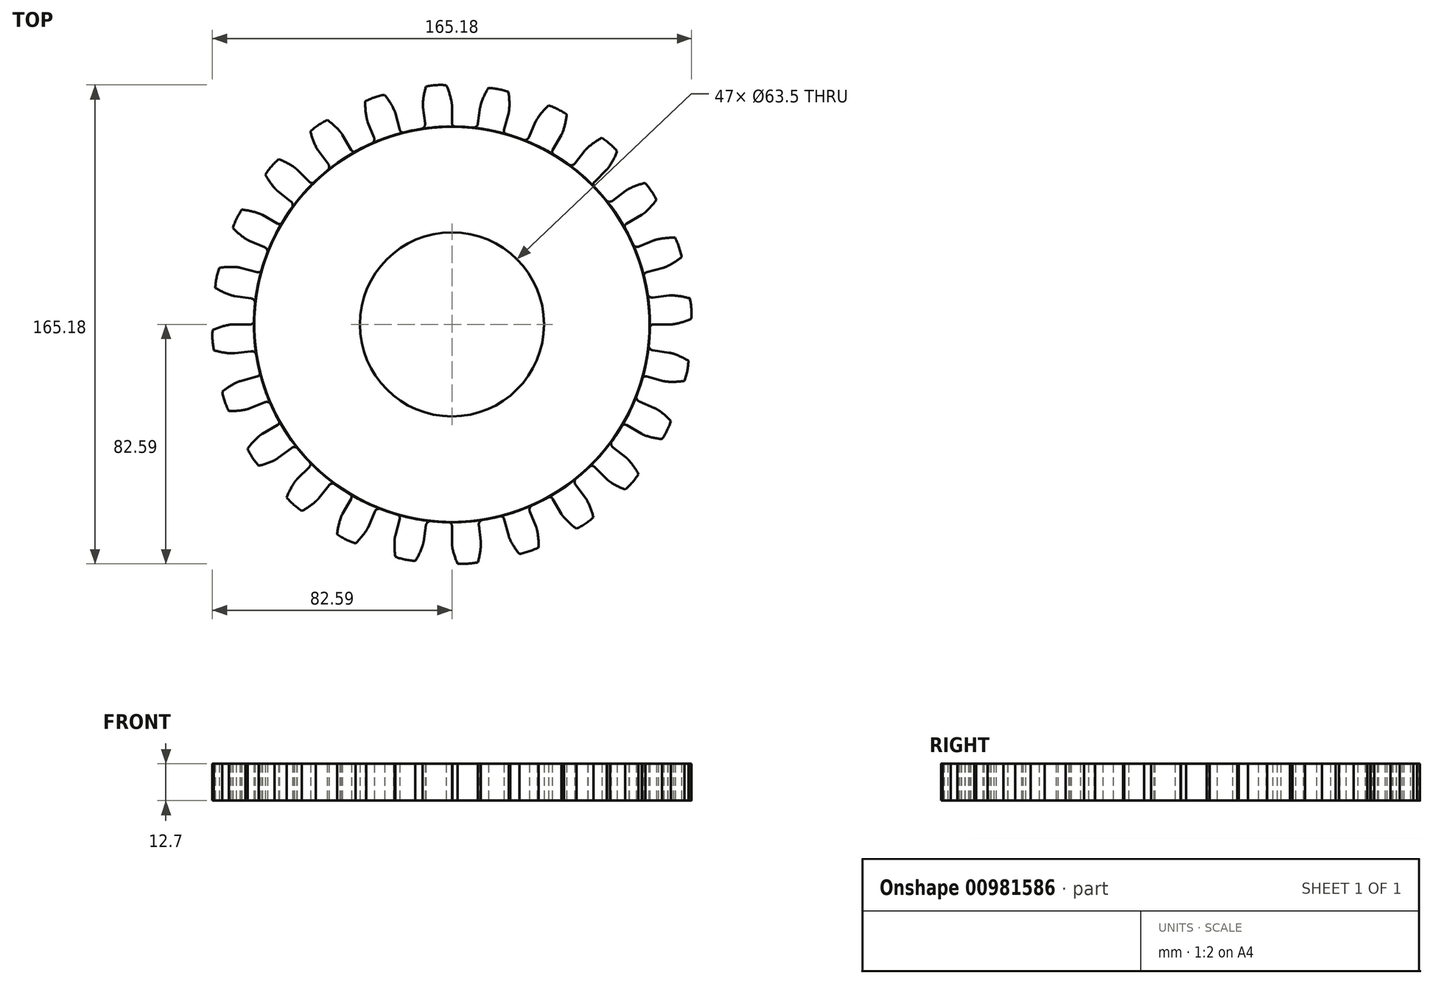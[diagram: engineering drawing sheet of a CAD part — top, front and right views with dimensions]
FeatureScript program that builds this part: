
annotation { "Feature Type Name" : "Feature", "Feature Type Description" : "" }
export const myFeature = defineFeature(function(context is Context, id is Id, definition is map)
    precondition{}
    {
        {
            var Q0;
            Q0=qCreatedBy(makeId("Top.planeOp"),FACE);
            var sketch = newSketch(context, id + "F0", { "sketchPlane" : qUnion([Q0])});
            skCircle(sketch, "E0", {"center": v(0, 0) * mm, "radius": 68.24 * mm});
            skCircle(sketch, "E1", {"center": v(0, 0) * mm, "radius": 76.2 * mm, "construction": true});
            skCircle(sketch, "E2", {"center": v(0, 0) * mm, "radius": 82.55 * mm, "construction": true});
            skLineSegment(sketch, "E3", {"start": v(0, 0) * mm, "end": v(0, 97.16) * mm, "construction": true});
            skLineSegment(sketch, "E4", {"start": v(0, 0) * mm, "end": v(-6.33, 96.56) * mm, "construction": true});
            skCircle(sketch, "E5", {"center": v(0, 0) * mm, "radius": 69.84 * mm, "construction": true});
            skCircle(sketch, "E6", {"center": v(0, 0) * mm, "radius": 75.54 * mm, "construction": true});
            skLineSegment(sketch, "E7", {"start": v(0, 0) * mm, "end": v(-12.68, 96.32) * mm, "construction": true});
            skLineSegment(sketch, "E8", {"start": v(0, 0) * mm, "end": v(-19.06, 95.82) * mm, "construction": true});
            skLineSegment(sketch, "E9", {"start": v(-4.94, 75.38) * mm, "end": v(0, 75.7) * mm, "construction": true});
            skPoint(sketch, "E10", {"position": v(-4.93, 75.38) * mm});
            skPoint(sketch, "E11", {"position": v(-4.94, 75.38) * mm});
            skLineSegment(sketch, "E12", {"start": v(-4.94, 75.38) * mm, "end": v(0, 75.54) * mm, "construction": true});
            skPoint(sketch, "E13", {"position": v(-9.86, 74.9) * mm});
            skLineSegment(sketch, "E14", {"start": v(-9.86, 74.9) * mm, "end": v(-0.04, 76.19) * mm, "construction": true});
            skLineSegment(sketch, "E15", {"start": v(-14.74, 74.09) * mm, "end": v(-0.16, 76.99) * mm, "construction": true});
            skArc(sketch, "E16", {"start": v(0, 75.7) * mm, "mid": v(-0.01, 75.94) * mm, "end": v(-0.04, 76.19) * mm});
            skArc(sketch, "E17", {"start": v(-0.04, 76.19) * mm, "mid": v(-0.1, 76.59) * mm, "end": v(-0.16, 76.99) * mm});
            skLineSegment(sketch, "E18", {"start": v(-0.04, 76.19) * mm, "end": v(-0.05, 76.26) * mm, "construction": true});
            skLineSegment(sketch, "E19", {"start": v(0, 75.7) * mm, "end": v(0, 75.86) * mm, "construction": true});
            skArc(sketch, "E20", {"start": v(0, 75.54) * mm, "mid": v(0, 75.62) * mm, "end": v(0, 75.7) * mm});
            skArc(sketch, "E21", {"start": v(-0.16, 76.99) * mm, "mid": v(-0.9, 79.8) * mm, "end": v(-1.95, 82.53) * mm});
            skLineSegment(sketch, "E22", {"start": v(-0.16, 76.99) * mm, "end": v(-0.27, 77.5) * mm, "construction": true});
            skPoint(sketch, "E23", {"position": v(-9.96, 74.88) * mm});
            skPoint(sketch, "E24", {"position": v(-4.99, 75.37) * mm});
            skLineSegment(sketch, "E25", {"start": v(0, 0) * mm, "end": v(-4.99, 75.37) * mm, "construction": true});
            skArc(sketch, "E26.MirrorCS", {"start": v(-9.98, 76.34) * mm, "mid": v(-9.63, 79.23) * mm, "end": v(-8.95, 82.06) * mm});
            skArc(sketch, "E27.MirrorCS", {"start": v(-10, 75.53) * mm, "mid": v(-10, 75.93) * mm, "end": v(-9.98, 76.34) * mm});
            skArc(sketch, "E28.MirrorCS", {"start": v(-9.98, 75.04) * mm, "mid": v(-10, 75.28) * mm, "end": v(-10, 75.53) * mm});
            skArc(sketch, "E29", {"start": v(-9.98, 75.04) * mm, "mid": v(-9.97, 74.96) * mm, "end": v(-9.96, 74.88) * mm});
            skLineSegment(sketch, "E30", {"start": v(-9.96, 74.88) * mm, "end": v(-9.26, 69.23) * mm});
            skLineSegment(sketch, "E31", {"start": v(0, 75.54) * mm, "end": v(0, 69.84) * mm});
            skArc(sketch, "E32", {"start": v(-1.95, 82.53) * mm, "mid": v(-5.5, 83) * mm, "end": v(-8.95, 82.06) * mm});
            skSolve(sketch);
        }
        {
            var Q0;
            Q0 = qSketchRegion(id + "F0", true);
            extrude(context, id + "F1", {"entities" : qUnion([Q0]), "depth" : 12.7 * mm, "offsetDistance" : 25.4 * mm});
        }
        {
            var Q0;
            Q0=qCreatedBy(makeId("Top.planeOp"),FACE);
            var sketch = newSketch(context, id + "F2", { "sketchPlane" : qUnion([Q0])});
            skArc(sketch, "E33", {"start": v(0, 75.7) * mm, "mid": v(-0.01, 75.94) * mm, "end": v(-0.04, 76.19) * mm});
            skArc(sketch, "E34", {"start": v(-0.04, 76.19) * mm, "mid": v(-0.1, 76.59) * mm, "end": v(-0.16, 76.99) * mm});
            skArc(sketch, "E35", {"start": v(0, 75.54) * mm, "mid": v(0, 75.62) * mm, "end": v(0, 75.7) * mm});
            skArc(sketch, "E36", {"start": v(-0.16, 76.99) * mm, "mid": v(-0.9, 79.8) * mm, "end": v(-1.95, 82.53) * mm});
            skArc(sketch, "E37.MirrorCS", {"start": v(-9.98, 76.34) * mm, "mid": v(-9.63, 79.23) * mm, "end": v(-8.95, 82.06) * mm});
            skArc(sketch, "E38.MirrorCS", {"start": v(-10, 75.53) * mm, "mid": v(-10, 75.93) * mm, "end": v(-9.98, 76.34) * mm});
            skArc(sketch, "E39.MirrorCS", {"start": v(-9.98, 75.04) * mm, "mid": v(-10, 75.28) * mm, "end": v(-10, 75.53) * mm});
            skArc(sketch, "E40", {"start": v(-9.98, 75.04) * mm, "mid": v(-9.97, 74.96) * mm, "end": v(-9.96, 74.88) * mm});
            skLineSegment(sketch, "E41", {"start": v(-9.97, 74.94) * mm, "end": v(-9.26, 69.27) * mm});
            skLineSegment(sketch, "E42", {"start": v(0, 75.54) * mm, "end": v(0, 69.51) * mm});
            skArc(sketch, "E43", {"start": v(-1.95, 82.53) * mm, "mid": v(-5.46, 82.54) * mm, "end": v(-8.95, 82.06) * mm});
            skArc(sketch, "E44", {"start": v(-10.67, 67.4) * mm, "mid": v(-9.59, 68.05) * mm, "end": v(-9.26, 69.27) * mm});
            skArc(sketch, "E45", {"start": v(0, 69.51) * mm, "mid": v(0.37, 68.61) * mm, "end": v(1.26, 68.23) * mm});
            skCircle(sketch, "E46.0", {"center": v(0, 0) * mm, "radius": 68.24 * mm});
            skSolve(sketch);
        }
        {
            var Q0;
            Q0=makeQuery(id+"F2.imprint","IMPRINT",FACE,{"disambiguationData":[TD([[makeQuery(id+"F2.imprint","IMPRINT",EDGE,{"derivedFrom":sQuery(id+"F2.wireOp",EDGE,"E33")}),1.0]])]});
            extrude(context, id + "F3", {"entities" : qUnion([Q0]), "operationType" : NewBodyOperationType.ADD, "depth" : 12.7 * mm, "offsetDistance" : 25.4 * mm});
        }
        {
            var Q0;
            Q0=makeQuery(id+"F1.opExtrude","SWEPT_BODY",BODY,{"disambiguationData":[OSD([sQuery(id+"F0.wireOp",EDGE,"E0")])]});
            var Q1;
            Q1=makeQuery(id+"F1.opExtrude","SWEPT_FACE",FACE,{"disambiguationData":[OSD([sQuery(id+"F0.wireOp",EDGE,"E0")])]});
            circularPattern(context, id + "F4", {"entities" : qUnion([Q0]), "axis" : qUnion([Q1]), "angle" : 360 * degree, "instanceCount" : 24, "equalSpace" : true, "isCentered" : true});
        }
        {
            var Q0;
            Q0=sQuery(id+"F0.wireOp",VERTEX,"E3.start");
            var Q1;
            Q1=makeQuery(id+"F1.opExtrude","SWEPT_BODY",BODY,{"disambiguationData":[OSD([sQuery(id+"F0.wireOp",EDGE,"E0")])]});
            var Q2;
            Q2=makeQuery(id+"F4.opPattern","COPY",BODY,{"derivedFrom":makeQuery(id+"F1.opExtrude","SWEPT_BODY",BODY,{"disambiguationData":[OSD([sQuery(id+"F0.wireOp",EDGE,"E0")])]}),"instanceName":"-23"});
            var Q3;
            Q3=makeQuery(id+"F4.opPattern","COPY",BODY,{"derivedFrom":makeQuery(id+"F1.opExtrude","SWEPT_BODY",BODY,{"disambiguationData":[OSD([sQuery(id+"F0.wireOp",EDGE,"E0")])]}),"instanceName":"-22"});
            var Q4;
            Q4=makeQuery(id+"F4.opPattern","COPY",BODY,{"derivedFrom":makeQuery(id+"F1.opExtrude","SWEPT_BODY",BODY,{"disambiguationData":[OSD([sQuery(id+"F0.wireOp",EDGE,"E0")])]}),"instanceName":"-21"});
            var Q5;
            Q5=makeQuery(id+"F4.opPattern","COPY",BODY,{"derivedFrom":makeQuery(id+"F1.opExtrude","SWEPT_BODY",BODY,{"disambiguationData":[OSD([sQuery(id+"F0.wireOp",EDGE,"E0")])]}),"instanceName":"-20"});
            var Q6;
            Q6=makeQuery(id+"F4.opPattern","COPY",BODY,{"derivedFrom":makeQuery(id+"F1.opExtrude","SWEPT_BODY",BODY,{"disambiguationData":[OSD([sQuery(id+"F0.wireOp",EDGE,"E0")])]}),"instanceName":"-19"});
            var Q7;
            Q7=makeQuery(id+"F4.opPattern","COPY",BODY,{"derivedFrom":makeQuery(id+"F1.opExtrude","SWEPT_BODY",BODY,{"disambiguationData":[OSD([sQuery(id+"F0.wireOp",EDGE,"E0")])]}),"instanceName":"-18"});
            var Q8;
            Q8=makeQuery(id+"F4.opPattern","COPY",BODY,{"derivedFrom":makeQuery(id+"F1.opExtrude","SWEPT_BODY",BODY,{"disambiguationData":[OSD([sQuery(id+"F0.wireOp",EDGE,"E0")])]}),"instanceName":"-17"});
            var Q9;
            Q9=makeQuery(id+"F4.opPattern","COPY",BODY,{"derivedFrom":makeQuery(id+"F1.opExtrude","SWEPT_BODY",BODY,{"disambiguationData":[OSD([sQuery(id+"F0.wireOp",EDGE,"E0")])]}),"instanceName":"-16"});
            var Q10;
            Q10=makeQuery(id+"F4.opPattern","COPY",BODY,{"derivedFrom":makeQuery(id+"F1.opExtrude","SWEPT_BODY",BODY,{"disambiguationData":[OSD([sQuery(id+"F0.wireOp",EDGE,"E0")])]}),"instanceName":"-15"});
            var Q11;
            Q11=makeQuery(id+"F4.opPattern","COPY",BODY,{"derivedFrom":makeQuery(id+"F1.opExtrude","SWEPT_BODY",BODY,{"disambiguationData":[OSD([sQuery(id+"F0.wireOp",EDGE,"E0")])]}),"instanceName":"-14"});
            var Q12;
            Q12=makeQuery(id+"F4.opPattern","COPY",BODY,{"derivedFrom":makeQuery(id+"F1.opExtrude","SWEPT_BODY",BODY,{"disambiguationData":[OSD([sQuery(id+"F0.wireOp",EDGE,"E0")])]}),"instanceName":"-13"});
            var Q13;
            Q13=makeQuery(id+"F4.opPattern","COPY",BODY,{"derivedFrom":makeQuery(id+"F1.opExtrude","SWEPT_BODY",BODY,{"disambiguationData":[OSD([sQuery(id+"F0.wireOp",EDGE,"E0")])]}),"instanceName":"-12"});
            var Q14;
            Q14=makeQuery(id+"F4.opPattern","COPY",BODY,{"derivedFrom":makeQuery(id+"F1.opExtrude","SWEPT_BODY",BODY,{"disambiguationData":[OSD([sQuery(id+"F0.wireOp",EDGE,"E0")])]}),"instanceName":"-11"});
            var Q15;
            Q15=makeQuery(id+"F4.opPattern","COPY",BODY,{"derivedFrom":makeQuery(id+"F1.opExtrude","SWEPT_BODY",BODY,{"disambiguationData":[OSD([sQuery(id+"F0.wireOp",EDGE,"E0")])]}),"instanceName":"-10"});
            var Q16;
            Q16=makeQuery(id+"F4.opPattern","COPY",BODY,{"derivedFrom":makeQuery(id+"F1.opExtrude","SWEPT_BODY",BODY,{"disambiguationData":[OSD([sQuery(id+"F0.wireOp",EDGE,"E0")])]}),"instanceName":"-9"});
            var Q17;
            Q17=makeQuery(id+"F4.opPattern","COPY",BODY,{"derivedFrom":makeQuery(id+"F1.opExtrude","SWEPT_BODY",BODY,{"disambiguationData":[OSD([sQuery(id+"F0.wireOp",EDGE,"E0")])]}),"instanceName":"-8"});
            var Q18;
            Q18=makeQuery(id+"F4.opPattern","COPY",BODY,{"derivedFrom":makeQuery(id+"F1.opExtrude","SWEPT_BODY",BODY,{"disambiguationData":[OSD([sQuery(id+"F0.wireOp",EDGE,"E0")])]}),"instanceName":"-7"});
            var Q19;
            Q19=makeQuery(id+"F4.opPattern","COPY",BODY,{"derivedFrom":makeQuery(id+"F1.opExtrude","SWEPT_BODY",BODY,{"disambiguationData":[OSD([sQuery(id+"F0.wireOp",EDGE,"E0")])]}),"instanceName":"-6"});
            var Q20;
            Q20=makeQuery(id+"F4.opPattern","COPY",BODY,{"derivedFrom":makeQuery(id+"F1.opExtrude","SWEPT_BODY",BODY,{"disambiguationData":[OSD([sQuery(id+"F0.wireOp",EDGE,"E0")])]}),"instanceName":"-5"});
            var Q21;
            Q21=makeQuery(id+"F4.opPattern","COPY",BODY,{"derivedFrom":makeQuery(id+"F1.opExtrude","SWEPT_BODY",BODY,{"disambiguationData":[OSD([sQuery(id+"F0.wireOp",EDGE,"E0")])]}),"instanceName":"-4"});
            var Q22;
            Q22=makeQuery(id+"F4.opPattern","COPY",BODY,{"derivedFrom":makeQuery(id+"F1.opExtrude","SWEPT_BODY",BODY,{"disambiguationData":[OSD([sQuery(id+"F0.wireOp",EDGE,"E0")])]}),"instanceName":"-3"});
            var Q23;
            Q23=makeQuery(id+"F4.opPattern","COPY",BODY,{"derivedFrom":makeQuery(id+"F1.opExtrude","SWEPT_BODY",BODY,{"disambiguationData":[OSD([sQuery(id+"F0.wireOp",EDGE,"E0")])]}),"instanceName":"-2"});
            var Q24;
            Q24=makeQuery(id+"F4.opPattern","COPY",BODY,{"derivedFrom":makeQuery(id+"F1.opExtrude","SWEPT_BODY",BODY,{"disambiguationData":[OSD([sQuery(id+"F0.wireOp",EDGE,"E0")])]}),"instanceName":"-1"});
            var Q25;
            Q25=makeQuery(id+"F4.opPattern","COPY",BODY,{"derivedFrom":makeQuery(id+"F1.opExtrude","SWEPT_BODY",BODY,{"disambiguationData":[OSD([sQuery(id+"F0.wireOp",EDGE,"E0")])]}),"instanceName":"1"});
            var Q26;
            Q26=makeQuery(id+"F4.opPattern","COPY",BODY,{"derivedFrom":makeQuery(id+"F1.opExtrude","SWEPT_BODY",BODY,{"disambiguationData":[OSD([sQuery(id+"F0.wireOp",EDGE,"E0")])]}),"instanceName":"2"});
            var Q27;
            Q27=makeQuery(id+"F4.opPattern","COPY",BODY,{"derivedFrom":makeQuery(id+"F1.opExtrude","SWEPT_BODY",BODY,{"disambiguationData":[OSD([sQuery(id+"F0.wireOp",EDGE,"E0")])]}),"instanceName":"3"});
            var Q28;
            Q28=makeQuery(id+"F4.opPattern","COPY",BODY,{"derivedFrom":makeQuery(id+"F1.opExtrude","SWEPT_BODY",BODY,{"disambiguationData":[OSD([sQuery(id+"F0.wireOp",EDGE,"E0")])]}),"instanceName":"4"});
            var Q29;
            Q29=makeQuery(id+"F4.opPattern","COPY",BODY,{"derivedFrom":makeQuery(id+"F1.opExtrude","SWEPT_BODY",BODY,{"disambiguationData":[OSD([sQuery(id+"F0.wireOp",EDGE,"E0")])]}),"instanceName":"5"});
            var Q30;
            Q30=makeQuery(id+"F4.opPattern","COPY",BODY,{"derivedFrom":makeQuery(id+"F1.opExtrude","SWEPT_BODY",BODY,{"disambiguationData":[OSD([sQuery(id+"F0.wireOp",EDGE,"E0")])]}),"instanceName":"6"});
            var Q31;
            Q31=makeQuery(id+"F4.opPattern","COPY",BODY,{"derivedFrom":makeQuery(id+"F1.opExtrude","SWEPT_BODY",BODY,{"disambiguationData":[OSD([sQuery(id+"F0.wireOp",EDGE,"E0")])]}),"instanceName":"7"});
            var Q32;
            Q32=makeQuery(id+"F4.opPattern","COPY",BODY,{"derivedFrom":makeQuery(id+"F1.opExtrude","SWEPT_BODY",BODY,{"disambiguationData":[OSD([sQuery(id+"F0.wireOp",EDGE,"E0")])]}),"instanceName":"8"});
            var Q33;
            Q33=makeQuery(id+"F4.opPattern","COPY",BODY,{"derivedFrom":makeQuery(id+"F1.opExtrude","SWEPT_BODY",BODY,{"disambiguationData":[OSD([sQuery(id+"F0.wireOp",EDGE,"E0")])]}),"instanceName":"9"});
            var Q34;
            Q34=makeQuery(id+"F4.opPattern","COPY",BODY,{"derivedFrom":makeQuery(id+"F1.opExtrude","SWEPT_BODY",BODY,{"disambiguationData":[OSD([sQuery(id+"F0.wireOp",EDGE,"E0")])]}),"instanceName":"10"});
            var Q35;
            Q35=makeQuery(id+"F4.opPattern","COPY",BODY,{"derivedFrom":makeQuery(id+"F1.opExtrude","SWEPT_BODY",BODY,{"disambiguationData":[OSD([sQuery(id+"F0.wireOp",EDGE,"E0")])]}),"instanceName":"11"});
            var Q36;
            Q36=makeQuery(id+"F4.opPattern","COPY",BODY,{"derivedFrom":makeQuery(id+"F1.opExtrude","SWEPT_BODY",BODY,{"disambiguationData":[OSD([sQuery(id+"F0.wireOp",EDGE,"E0")])]}),"instanceName":"12"});
            var Q37;
            Q37=makeQuery(id+"F4.opPattern","COPY",BODY,{"derivedFrom":makeQuery(id+"F1.opExtrude","SWEPT_BODY",BODY,{"disambiguationData":[OSD([sQuery(id+"F0.wireOp",EDGE,"E0")])]}),"instanceName":"13"});
            var Q38;
            Q38=makeQuery(id+"F4.opPattern","COPY",BODY,{"derivedFrom":makeQuery(id+"F1.opExtrude","SWEPT_BODY",BODY,{"disambiguationData":[OSD([sQuery(id+"F0.wireOp",EDGE,"E0")])]}),"instanceName":"14"});
            var Q39;
            Q39=makeQuery(id+"F4.opPattern","COPY",BODY,{"derivedFrom":makeQuery(id+"F1.opExtrude","SWEPT_BODY",BODY,{"disambiguationData":[OSD([sQuery(id+"F0.wireOp",EDGE,"E0")])]}),"instanceName":"15"});
            var Q40;
            Q40=makeQuery(id+"F4.opPattern","COPY",BODY,{"derivedFrom":makeQuery(id+"F1.opExtrude","SWEPT_BODY",BODY,{"disambiguationData":[OSD([sQuery(id+"F0.wireOp",EDGE,"E0")])]}),"instanceName":"16"});
            var Q41;
            Q41=makeQuery(id+"F4.opPattern","COPY",BODY,{"derivedFrom":makeQuery(id+"F1.opExtrude","SWEPT_BODY",BODY,{"disambiguationData":[OSD([sQuery(id+"F0.wireOp",EDGE,"E0")])]}),"instanceName":"17"});
            var Q42;
            Q42=makeQuery(id+"F4.opPattern","COPY",BODY,{"derivedFrom":makeQuery(id+"F1.opExtrude","SWEPT_BODY",BODY,{"disambiguationData":[OSD([sQuery(id+"F0.wireOp",EDGE,"E0")])]}),"instanceName":"18"});
            var Q43;
            Q43=makeQuery(id+"F4.opPattern","COPY",BODY,{"derivedFrom":makeQuery(id+"F1.opExtrude","SWEPT_BODY",BODY,{"disambiguationData":[OSD([sQuery(id+"F0.wireOp",EDGE,"E0")])]}),"instanceName":"19"});
            var Q44;
            Q44=makeQuery(id+"F4.opPattern","COPY",BODY,{"derivedFrom":makeQuery(id+"F1.opExtrude","SWEPT_BODY",BODY,{"disambiguationData":[OSD([sQuery(id+"F0.wireOp",EDGE,"E0")])]}),"instanceName":"20"});
            var Q45;
            Q45=makeQuery(id+"F4.opPattern","COPY",BODY,{"derivedFrom":makeQuery(id+"F1.opExtrude","SWEPT_BODY",BODY,{"disambiguationData":[OSD([sQuery(id+"F0.wireOp",EDGE,"E0")])]}),"instanceName":"21"});
            var Q46;
            Q46=makeQuery(id+"F4.opPattern","COPY",BODY,{"derivedFrom":makeQuery(id+"F1.opExtrude","SWEPT_BODY",BODY,{"disambiguationData":[OSD([sQuery(id+"F0.wireOp",EDGE,"E0")])]}),"instanceName":"22"});
            var Q47;
            Q47=makeQuery(id+"F4.opPattern","COPY",BODY,{"derivedFrom":makeQuery(id+"F1.opExtrude","SWEPT_BODY",BODY,{"disambiguationData":[OSD([sQuery(id+"F0.wireOp",EDGE,"E0")])]}),"instanceName":"23"});
            hole(context, id + "F5", {"style" : HoleStyle.SIMPLE, "endStyle" : HoleEndStyle.THROUGH, "oppositeDirection" : true, "holeDiameter" : 63.5 * mm, "majorDiameter" : 6.35 * mm, "isTappedThrough" : true, "tappedDepth" : 12.7 * mm, "tapClearance" : 3, "locations" : qUnion([Q0]), "scope" : qUnion([Q1, Q2, Q3, Q4, Q5, Q6, Q7, Q8, Q9, Q10, Q11, Q12, Q13, Q14, Q15, Q16, Q17, Q18, Q19, Q20, Q21, Q22, Q23, Q24, Q25, Q26, Q27, Q28, Q29, Q30, Q31, Q32, Q33, Q34, Q35, Q36, Q37, Q38, Q39, Q40, Q41, Q42, Q43, Q44, Q45, Q46, Q47])});
        }
    });
